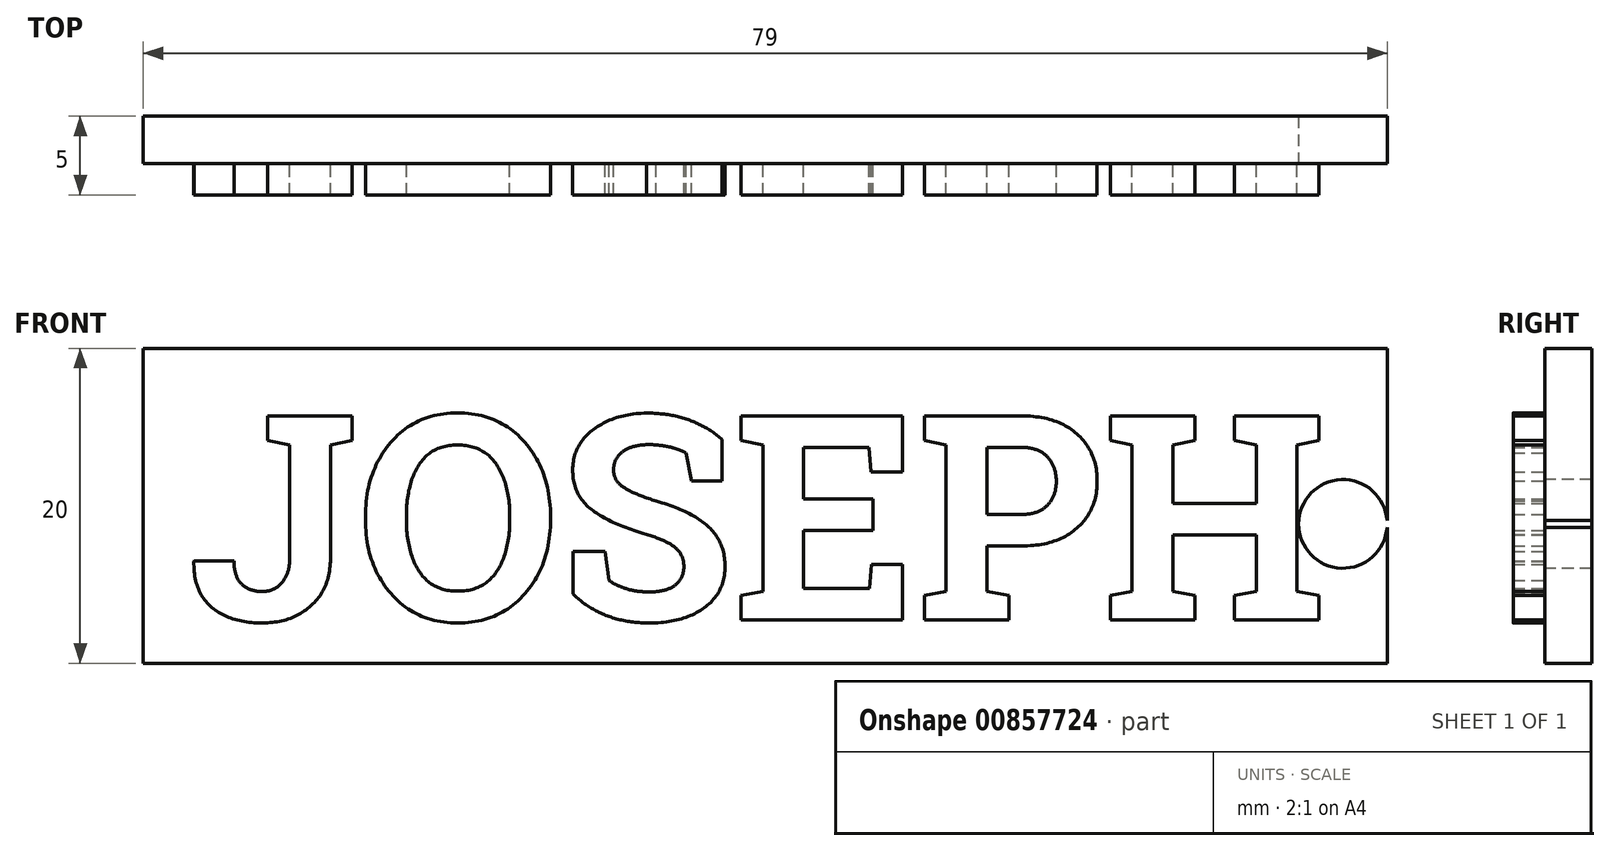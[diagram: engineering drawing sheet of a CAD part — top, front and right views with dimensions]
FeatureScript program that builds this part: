
annotation { "Feature Type Name" : "Feature", "Feature Type Description" : "" }
export const myFeature = defineFeature(function(context is Context, id is Id, definition is map)
    precondition{}
    {
        {
            var Q0;
            Q0=qCreatedBy(makeId("Front.planeOp"),FACE);
            var sketch = newSketch(context, id + "F0", { "sketchPlane" : qUnion([Q0])});
            skLineSegment(sketch, "E0.bottom", {"start": v(0, 0) * mm, "end": v(79, 0) * mm});
            skLineSegment(sketch, "E0.top", {"start": v(0, -20) * mm, "end": v(79, -20) * mm});
            skLineSegment(sketch, "E0.left", {"start": v(0, 0) * mm, "end": v(0, -20) * mm});
            skLineSegment(sketch, "E0.right", {"start": v(79, 0) * mm, "end": v(79, -20) * mm});
            skSolve(sketch);
        }
        {
            var Q0;
            Q0 = qSketchRegion(id + "F0", true);
            extrude(context, id + "F1", {"entities" : qUnion([Q0]), "depth" : 3 * mm, "offsetDistance" : 25.4 * mm});
        }
        {
            var Q0;
            Q0=makeQuery(id+"F1.opExtrude","CAP_FACE",FACE,{"disambiguationData":[OSD([sQuery(id+"F0.wireOp",EDGE,"E0.bottom"),sQuery(id+"F0.wireOp",EDGE,"E0.top"),sQuery(id+"F0.wireOp",EDGE,"E0.left"),sQuery(id+"F0.wireOp",EDGE,"E0.right")])],"isStart":false});
            var sketch = newSketch(context, id + "F2", { "sketchPlane" : qUnion([Q0])});
            skText(sketch, "E1", { "text": "JOSEPH", "fontName": "RobotoSlab-Bold.ttf"});
            const initialGuessF2  = {"E1": [0.0029, -0.01725, 1, 0, 0.01313]};
            skSetInitialGuess(sketch, initialGuessF2);
            skSolve(sketch);
        }
        {
            var Q0;
            Q0 = qSketchRegion(id + "F2", true);
            extrude(context, id + "F3", {"entities" : qUnion([Q0]), "operationType" : NewBodyOperationType.ADD, "depth" : 2 * mm, "offsetDistance" : 25.4 * mm});
        }
        {
            var Q0;
            {var subQ0=sQuery(id+"F0.wireOp",EDGE,"E0.top");var subQ1=sQuery(id+"F0.wireOp",EDGE,"E0.right");var subQ2=sQuery(id+"F0.wireOp",EDGE,"E0.bottom");var subQ3=sQuery(id+"F0.wireOp",EDGE,"E0.left");Q0=makeQuery(id+"F3.boolean.opBoolean","SPLIT",FACE,{"disambiguationData":[TD([makeQuery(id+"F1.opExtrude","SWEPT_FACE",FACE,{"disambiguationData":[OSD([subQ2])]})])],"derivedFrom":makeQuery(id+"F1.opExtrude","CAP_FACE",FACE,{"disambiguationData":[OSD([subQ2,subQ0,subQ3,subQ1])],"isStart":false})});}
            var sketch = newSketch(context, id + "F4", { "sketchPlane" : qUnion([Q0])});
            skSolve(sketch);
        }
        {
            var Q0;
            Q0=makeQuery(id+"F4.imprint","IMPRINT",FACE,{"disambiguationData":[TD([[makeQuery(id+"F4.imprint","IMPRINT",EDGE,{"derivedFrom":makeQuery(id+"F1.opExtrude","CAP_EDGE",EDGE,{"disambiguationData":[OSD([sQuery(id+"F0.wireOp",EDGE,"E0.bottom")])],"isStart":false})}),-1.0]])]});
            var sketch = newSketch(context, id + "F5", { "sketchPlane" : qUnion([Q0])});
            skCircle(sketch, "E2", {"center": v(76.2, -11.15) * mm, "radius": 2.82 * mm});
            skSolve(sketch);
        }
        {
            var Q0;
            Q0 = qSketchRegion(id + "F5", true);
            extrude(context, id + "F6", {"entities" : qUnion([Q0]), "operationType" : NewBodyOperationType.REMOVE, "oppositeDirection" : true, "depth" : 25.4 * mm, "offsetDistance" : 25.4 * mm});
        }
    });
